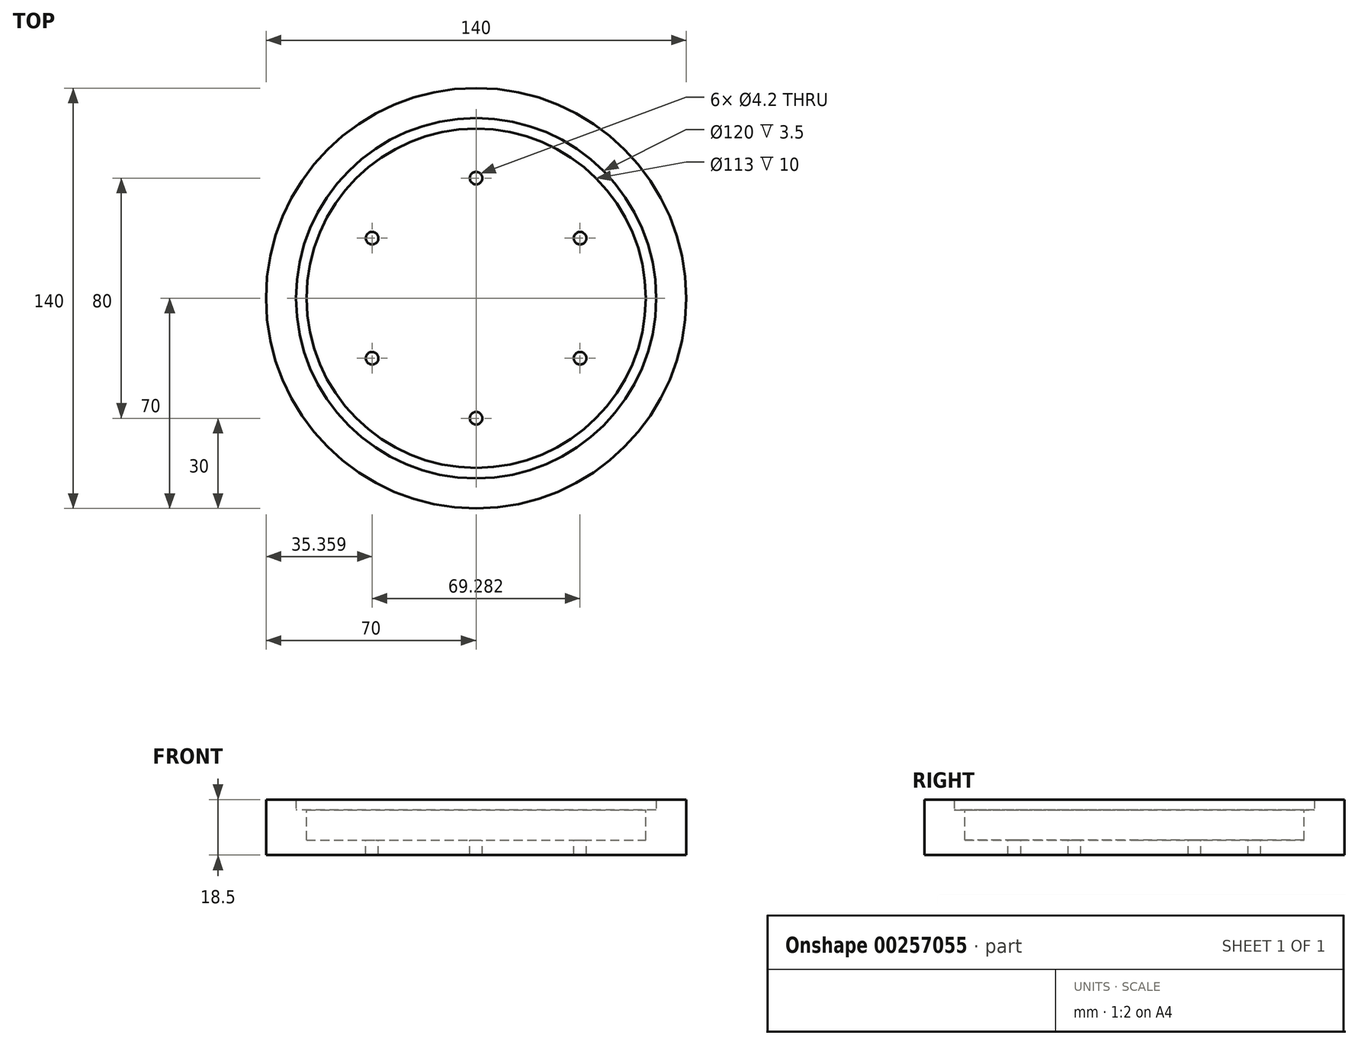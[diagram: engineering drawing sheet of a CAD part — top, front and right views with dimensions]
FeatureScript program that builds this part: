
annotation { "Feature Type Name" : "Feature", "Feature Type Description" : "" }
export const myFeature = defineFeature(function(context is Context, id is Id, definition is map)
    precondition{}
    {
        {
            var Q0;
            Q0=qCreatedBy(makeId("Top.planeOp"),FACE);
            var sketch = newSketch(context, id + "F0", { "sketchPlane" : qUnion([Q0])});
            skCircle(sketch, "E0", {"center": v(0, 0) * mm, "radius": 70 * mm});
            skCircle(sketch, "E1", {"center": v(0, 0) * mm, "radius": 60 * mm});
            skSolve(sketch);
        }
        {
            var Q0;
            Q0 = qSketchRegion(id + "F0", true);
            extrude(context, id + "F1", {"entities" : qUnion([Q0]), "depth" : 3.5 * mm});
        }
        {
            var Q0;
            Q0=makeQuery(id+"F1.opExtrude","CAP_FACE",FACE,{"disambiguationData":[OSD([sQuery(id+"F0.wireOp",EDGE,"E0"),sQuery(id+"F0.wireOp",EDGE,"E1")])],"isStart":true});
            var sketch = newSketch(context, id + "F2", { "sketchPlane" : qUnion([Q0])});
            skCircle(sketch, "E2", {"center": v(0, 0) * mm, "radius": 70 * mm});
            skCircle(sketch, "E3", {"center": v(0, 0) * mm, "radius": 56.5 * mm});
            skSolve(sketch);
        }
        {
            var Q0;
            Q0 = qSketchRegion(id + "F2", true);
            extrude(context, id + "F3", {"entities" : qUnion([Q0]), "operationType" : NewBodyOperationType.ADD, "depth" : 5 * mm});
        }
        {
            var Q0;
            Q0=makeQuery(id+"F3.opExtrude","CAP_FACE",FACE,{"disambiguationData":[OSD([sQuery(id+"F2.wireOp",EDGE,"E2"),sQuery(id+"F2.wireOp",EDGE,"E3")])],"isStart":false});
            var sketch = newSketch(context, id + "F4", { "sketchPlane" : qUnion([Q0])});
            skCircle(sketch, "E4", {"center": v(0, 0) * mm, "radius": 70 * mm});
            skCircle(sketch, "E5", {"center": v(0, 0) * mm, "radius": 56.5 * mm});
            skSolve(sketch);
        }
        {
            var Q0;
            Q0 = qSketchRegion(id + "F4", true);
            extrude(context, id + "F5", {"entities" : qUnion([Q0]), "operationType" : NewBodyOperationType.ADD, "depth" : 5 * mm});
        }
        {
            var Q0;
            Q0=makeQuery(id+"F5.opExtrude","CAP_FACE",FACE,{"disambiguationData":[OSD([sQuery(id+"F4.wireOp",EDGE,"E4"),sQuery(id+"F4.wireOp",EDGE,"E5")])],"isStart":false});
            var sketch = newSketch(context, id + "F6", { "sketchPlane" : qUnion([Q0])});
            skCircle(sketch, "E6", {"center": v(0, 0) * mm, "radius": 70 * mm});
            skCircle(sketch, "E7.cCircle", {"center": v(0, 0) * mm, "radius": 40 * mm, "construction": true});
            skLineSegment(sketch, "E7.0", {"start": v(0, -40) * mm, "end": v(-1.82, -38.95) * mm});
            skLineSegment(sketch, "E7.1", {"start": v(-34.64, -20) * mm, "end": v(-34.64, -17.9) * mm});
            skLineSegment(sketch, "E7.2", {"start": v(-34.64, 20) * mm, "end": v(-32.82, 21.05) * mm});
            skLineSegment(sketch, "E7.3", {"start": v(0, 40) * mm, "end": v(1.82, 38.95) * mm});
            skLineSegment(sketch, "E7.4", {"start": v(34.64, 20) * mm, "end": v(34.64, 17.9) * mm});
            skLineSegment(sketch, "E7.5", {"start": v(34.64, -20) * mm, "end": v(32.82, -21.05) * mm});
            skCircle(sketch, "E8", {"center": v(0, 40) * mm, "radius": 2.1 * mm});
            skCircle(sketch, "E9", {"center": v(34.64, 20) * mm, "radius": 2.1 * mm});
            skCircle(sketch, "E10", {"center": v(-34.64, 20) * mm, "radius": 2.1 * mm});
            skCircle(sketch, "E11", {"center": v(-34.64, -20) * mm, "radius": 2.1 * mm});
            skCircle(sketch, "E12", {"center": v(0, -40) * mm, "radius": 2.1 * mm});
            skCircle(sketch, "E13", {"center": v(34.64, -20) * mm, "radius": 2.1 * mm});
            skLineSegment(sketch, "E14.trimOffspring", {"start": v(-1.82, 38.95) * mm, "end": v(0, 40) * mm});
            skLineSegment(sketch, "E15.trimOffspring", {"start": v(-34.64, 17.9) * mm, "end": v(-34.64, 20) * mm});
            skLineSegment(sketch, "E16.trimOffspring", {"start": v(-32.82, -21.05) * mm, "end": v(-34.64, -20) * mm});
            skLineSegment(sketch, "E17.trimOffspring", {"start": v(1.82, -38.95) * mm, "end": v(0, -40) * mm});
            skLineSegment(sketch, "E18.trimOffspring", {"start": v(34.64, -17.9) * mm, "end": v(34.64, -20) * mm});
            skLineSegment(sketch, "E19.trimOffspring", {"start": v(32.82, 21.05) * mm, "end": v(34.64, 20) * mm});
            skSolve(sketch);
        }
        {
            var Q0;
            Q0 = qSketchRegion(id + "F6", true);
            extrude(context, id + "F7", {"entities" : qUnion([Q0]), "operationType" : NewBodyOperationType.ADD, "depth" : 5 * mm});
        }
    });
